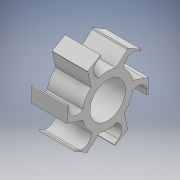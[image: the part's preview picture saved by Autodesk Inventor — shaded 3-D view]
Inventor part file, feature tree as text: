
AUTODESK INVENTOR PART (.ipt)
format: ipt  version: 2018 (Build 220112000, 112)  size: 170,496 bytes
history: native  units: mm
features: extrude x2, sketch x2, fillet x1, pattern_circular x1
ambient origin geometry x8: Origin, YZ Plane, XZ Plane, XY Plane, X Axis, Y Axis, Z Axis, Center Point
bodies: Solid1 (feature_tree)
feature tree (6):
  extrude  "Extrusion1"  Depth=3.5mm
  extrude  "Extrusion2"  Depth=0.125mm
  fillet  "Fillet1"  Radius=0.25mm
  pattern_circular  "Circular Pattern1"  [2 undecoded]
  sketch  "Sketch1"  dims[d0=3.5mm d1=5.0mm]
  sketch  "Sketch2"  dims[d2=3.5mm d3=0.0mm d4=0.125mm d5=0.25mm d6=0.5mm d11=0.5mm d12=1.0mm d14=1.0mm d15=0.9mm d16=1.5mm d17=0.125mm d18=3.5mm d19=0.0mm d20=2.0mm d21=60.0mm d22=360.0deg]
note: 2 required parameter values undecoded (feature->parameter linkage not recoverable at this tier; creation-order binding heuristic only, values carry confidence <= 0.55)
